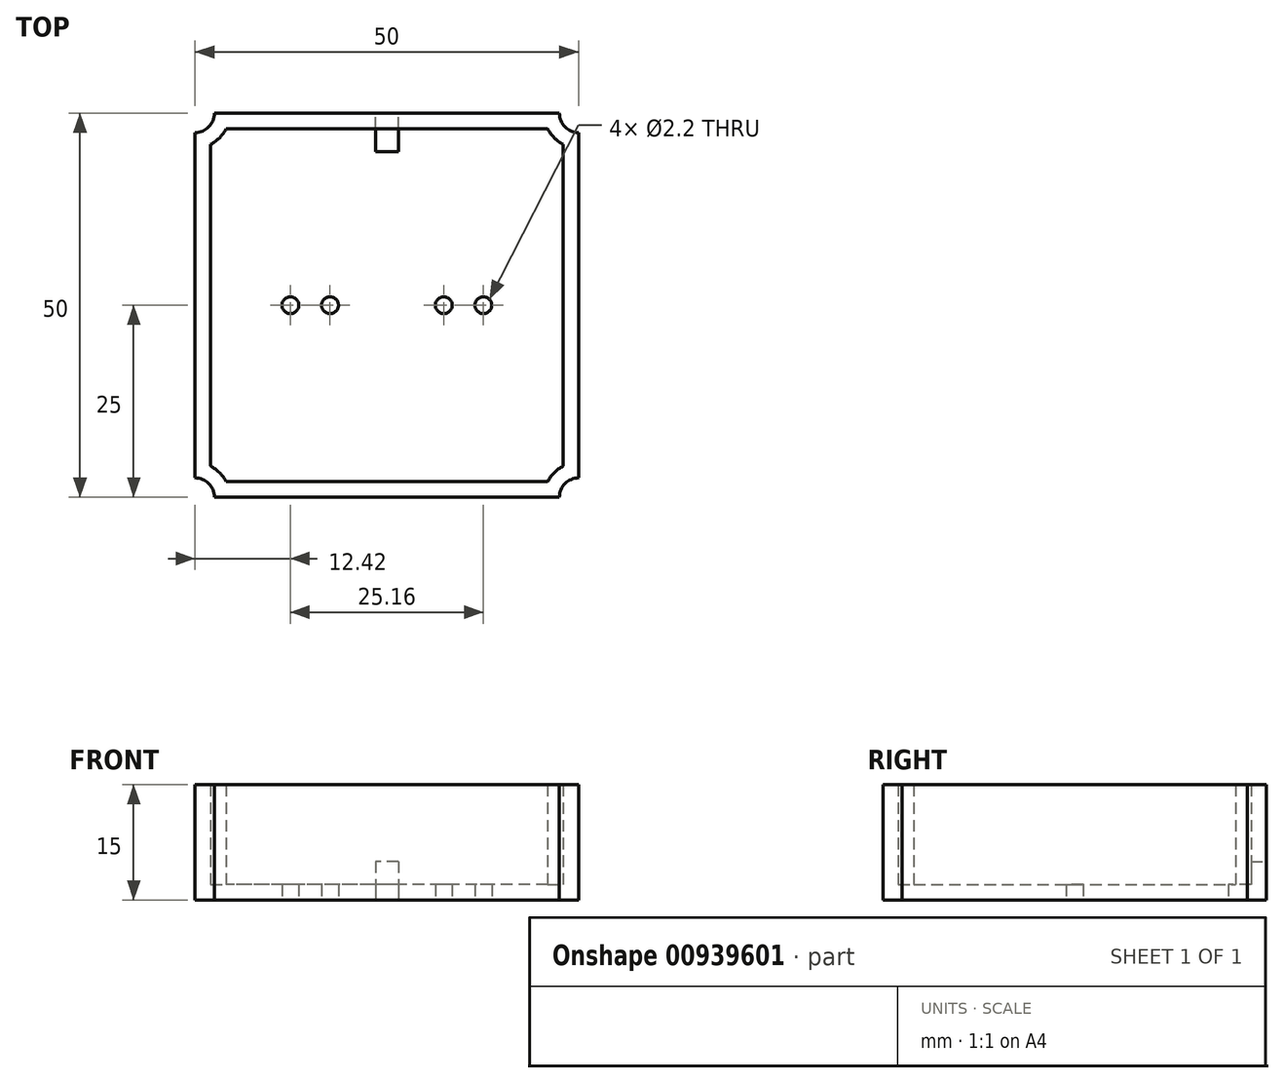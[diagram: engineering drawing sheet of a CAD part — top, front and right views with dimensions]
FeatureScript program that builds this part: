
annotation { "Feature Type Name" : "Feature", "Feature Type Description" : "" }
export const myFeature = defineFeature(function(context is Context, id is Id, definition is map)
    precondition{}
    {
        {
            var Q0;
            Q0=qCreatedBy(makeId("Top.planeOp"),FACE);
            var sketch = newSketch(context, id + "F0", { "sketchPlane" : qUnion([Q0])});
            skLineSegment(sketch, "E0.bottom", {"start": v(22.5, -25) * mm, "end": v(-22.5, -25) * mm});
            skLineSegment(sketch, "E0.top", {"start": v(25, 25) * mm, "end": v(-22.5, 25) * mm});
            skLineSegment(sketch, "E0.left", {"start": v(25, -22.5) * mm, "end": v(25, 22.5) * mm});
            skLineSegment(sketch, "E0.right", {"start": v(-25, -22.5) * mm, "end": v(-25, 22.5) * mm});
            skPoint(sketch, "E0.middle", {"position": v(0, 0) * mm});
            skArc(sketch, "E1", {"start": v(-25, 22.5) * mm, "mid": v(-23.23, 23.23) * mm, "end": v(-22.5, 25) * mm});
            skArc(sketch, "E2", {"start": v(22.5, 25) * mm, "mid": v(23.23, 23.23) * mm, "end": v(25, 22.5) * mm});
            skArc(sketch, "E3", {"start": v(25, -22.5) * mm, "mid": v(23.23, -23.23) * mm, "end": v(22.5, -25) * mm});
            skArc(sketch, "E4", {"start": v(-22.5, -25) * mm, "mid": v(-23.23, -23.23) * mm, "end": v(-25, -22.5) * mm});
            skArc(sketch, "E5", {"start": v(-12.58, 0) * mm, "mid": v(-12.52, -0.55) * mm, "end": v(-12.35, -1.07) * mm});
            skCircle(sketch, "E6", {"center": v(-12.58, 0) * mm, "radius": 1.1 * mm});
            skCircle(sketch, "E7", {"center": v(-7.42, 0) * mm, "radius": 1.1 * mm});
            skCircle(sketch, "E8", {"center": v(7.42, 0) * mm, "radius": 1.1 * mm});
            skCircle(sketch, "E9", {"center": v(12.58, 0) * mm, "radius": 1.1 * mm});
            skPoint(sketch, "E10.center.orphan", {"position": v(10, 0) * mm});
            skPoint(sketch, "E11.top.start.orphan", {"position": v(-10, 15) * mm});
            skPoint(sketch, "E12.orphan", {"position": v(10, 15) * mm});
            skPoint(sketch, "E11.bottom.end.orphan", {"position": v(10, -15) * mm});
            skPoint(sketch, "E11.left.start.orphan", {"position": v(-10, -15) * mm});
            skSolve(sketch);
        }
        {
            var Q0;
            Q0 = qSketchRegion(id + "F0", true);
            extrude(context, id + "F1", {"entities" : qUnion([Q0]), "depth" : 5 * mm, "offsetDistance" : 25 * mm});
        }
        {
            var Q0;
            Q0=makeQuery(id+"F1.opExtrude","CAP_FACE",FACE,{"disambiguationData":[OSD([sQuery(id+"F0.wireOp",EDGE,"E0.bottom"),sQuery(id+"F0.wireOp",EDGE,"E0.top"),sQuery(id+"F0.wireOp",EDGE,"E0.left"),sQuery(id+"F0.wireOp",EDGE,"E0.right"),sQuery(id+"F0.wireOp",EDGE,"E1"),sQuery(id+"F0.wireOp",EDGE,"E2"),sQuery(id+"F0.wireOp",EDGE,"E3"),sQuery(id+"F0.wireOp",EDGE,"E4"),sQuery(id+"F0.wireOp",EDGE,"E6"),sQuery(id+"F0.wireOp",EDGE,"E7"),sQuery(id+"F0.wireOp",EDGE,"E8"),sQuery(id+"F0.wireOp",EDGE,"E9")])],"isStart":false});
            extrude(context, id + "F2", {"entities" : qUnion([Q0]), "operationType" : NewBodyOperationType.ADD, "depth" : 10 * mm, "offsetDistance" : 25 * mm});
        }
        {
            var Q0;
            {var subQ0=sQuery(id+"F0.wireOp",EDGE,"E6");Q0=makeQuery(id+"F2.boolean.opBoolean","MERGE",FACE,{"derivedFrom":[makeQuery(id+"F1.opExtrude","SWEPT_FACE",FACE,{"disambiguationData":[OSD([subQ0])]}),makeQuery(id+"F2.opExtrude","SWEPT_FACE",FACE,{"disambiguationData":[OSD([subQ0])]})]});}
            var Q1;
            Q1=makeQuery(id+"F2.opExtrude","CAP_FACE",FACE,{"disambiguationData":[OSD([sQuery(id+"F0.wireOp",EDGE,"E0.bottom"),sQuery(id+"F0.wireOp",EDGE,"E0.top"),sQuery(id+"F0.wireOp",EDGE,"E0.left"),sQuery(id+"F0.wireOp",EDGE,"E0.right"),sQuery(id+"F0.wireOp",EDGE,"E1"),sQuery(id+"F0.wireOp",EDGE,"E2"),sQuery(id+"F0.wireOp",EDGE,"E3"),sQuery(id+"F0.wireOp",EDGE,"E4"),sQuery(id+"F0.wireOp",EDGE,"E6"),sQuery(id+"F0.wireOp",EDGE,"E7"),sQuery(id+"F0.wireOp",EDGE,"E8"),sQuery(id+"F0.wireOp",EDGE,"E9")])],"isStart":false});
            var Q2;
            {var subQ0=sQuery(id+"F0.wireOp",EDGE,"E9");Q2=makeQuery(id+"F2.boolean.opBoolean","MERGE",FACE,{"derivedFrom":[makeQuery(id+"F1.opExtrude","SWEPT_FACE",FACE,{"disambiguationData":[OSD([subQ0])]}),makeQuery(id+"F2.opExtrude","SWEPT_FACE",FACE,{"disambiguationData":[OSD([subQ0])]})]});}
            var Q3;
            {var subQ0=sQuery(id+"F0.wireOp",EDGE,"E8");Q3=makeQuery(id+"F2.boolean.opBoolean","MERGE",FACE,{"derivedFrom":[makeQuery(id+"F1.opExtrude","SWEPT_FACE",FACE,{"disambiguationData":[OSD([subQ0])]}),makeQuery(id+"F2.opExtrude","SWEPT_FACE",FACE,{"disambiguationData":[OSD([subQ0])]})]});}
            var Q4;
            {var subQ0=sQuery(id+"F0.wireOp",EDGE,"E7");Q4=makeQuery(id+"F2.boolean.opBoolean","MERGE",FACE,{"derivedFrom":[makeQuery(id+"F1.opExtrude","SWEPT_FACE",FACE,{"disambiguationData":[OSD([subQ0])]}),makeQuery(id+"F2.opExtrude","SWEPT_FACE",FACE,{"disambiguationData":[OSD([subQ0])]})]});}
            shell(context, id + "F3", {"entities" : qUnion([Q0, Q1, Q2, Q3, Q4]), "thickness" : 2 * mm});
        }
        {
            var Q0;
            Q0=qCreatedBy(makeId("Top.planeOp"),FACE);
            var sketch = newSketch(context, id + "F4", { "sketchPlane" : qUnion([Q0])});
            skLineSegment(sketch, "E13.bottom", {"start": v(-1.5, 20.01) * mm, "end": v(1.5, 20.01) * mm});
            skLineSegment(sketch, "E13.top", {"start": v(-1.5, 30.01) * mm, "end": v(1.5, 30.01) * mm});
            skLineSegment(sketch, "E13.left", {"start": v(-1.5, 20.01) * mm, "end": v(-1.5, 30.01) * mm});
            skLineSegment(sketch, "E13.right", {"start": v(1.5, 20.01) * mm, "end": v(1.5, 30.01) * mm});
            skPoint(sketch, "E13.middle", {"position": v(0, 25.01) * mm});
            skSolve(sketch);
        }
        {
            var Q0;
            Q0 = qSketchRegion(id + "F4", true);
            extrude(context, id + "F5", {"entities" : qUnion([Q0]), "operationType" : NewBodyOperationType.REMOVE, "depth" : 5 * mm, "offsetDistance" : 25 * mm});
        }
    });
